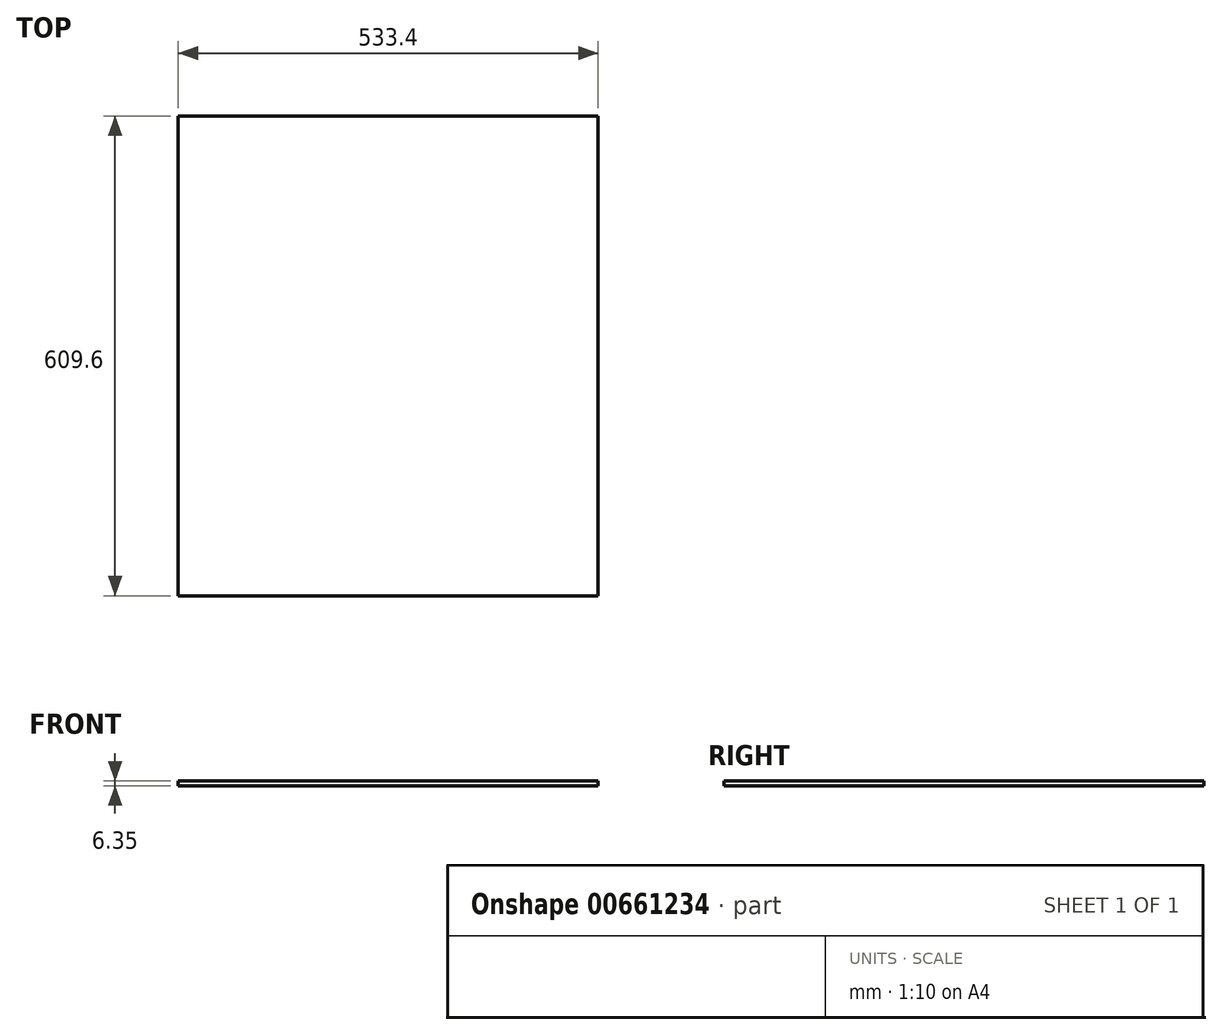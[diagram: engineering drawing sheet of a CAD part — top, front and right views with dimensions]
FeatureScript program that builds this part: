
annotation { "Feature Type Name" : "Feature", "Feature Type Description" : "" }
export const myFeature = defineFeature(function(context is Context, id is Id, definition is map)
    precondition{}
    {
        {
            var Q0;
            Q0=qCreatedBy(makeId("Top.planeOp"),FACE);
            var sketch = newSketch(context, id + "F0", { "sketchPlane" : qUnion([Q0])});
            skLineSegment(sketch, "E0.bottom", {"start": v(-499.53, 556.69) * mm, "end": v(33.87, 556.69) * mm});
            skLineSegment(sketch, "E0.top", {"start": v(-499.53, -52.91) * mm, "end": v(33.87, -52.91) * mm});
            skLineSegment(sketch, "E0.left", {"start": v(-499.53, 556.69) * mm, "end": v(-499.53, -52.91) * mm});
            skLineSegment(sketch, "E0.right", {"start": v(33.87, 556.69) * mm, "end": v(33.87, -52.91) * mm});
            skSolve(sketch);
        }
        {
            var Q0;
            Q0=makeQuery(id+"F0.imprint","IMPRINT",FACE,{"disambiguationData":[TD([[makeQuery(id+"F0.imprint","IMPRINT",EDGE,{"derivedFrom":sQuery(id+"F0.wireOp",EDGE,"E0.bottom")}),-1.0]])]});
            extrude(context, id + "F1", {"entities" : qUnion([Q0]), "depth" : 6.35 * mm, "offsetDistance" : 25.4 * mm});
        }
    });
